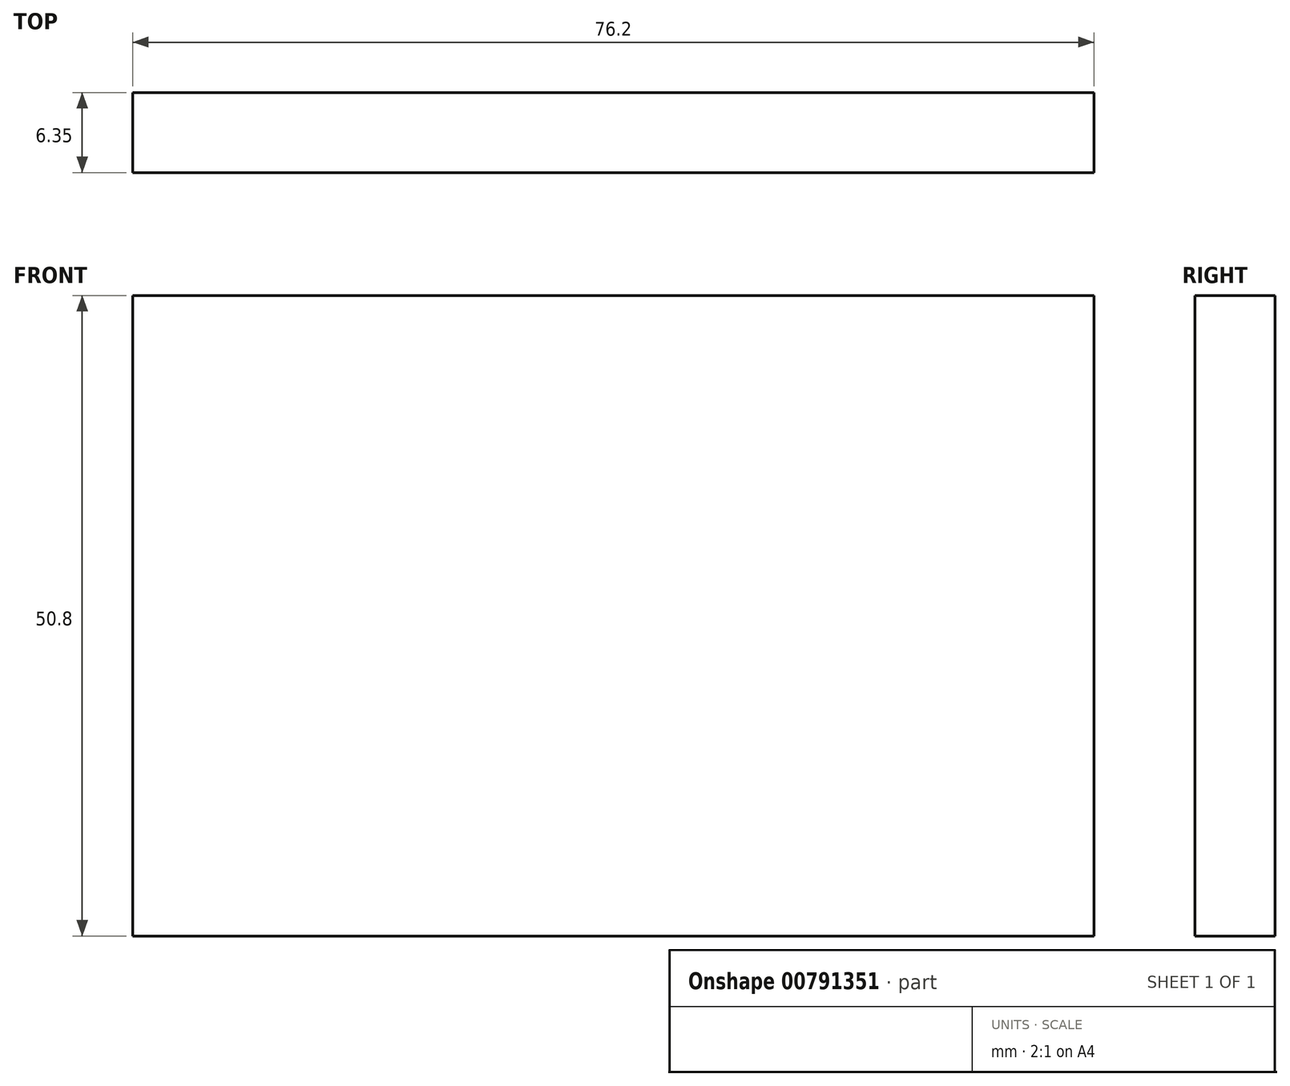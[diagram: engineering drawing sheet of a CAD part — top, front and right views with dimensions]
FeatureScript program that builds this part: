
annotation { "Feature Type Name" : "Feature", "Feature Type Description" : "" }
export const myFeature = defineFeature(function(context is Context, id is Id, definition is map)
    precondition{}
    {
        {
            var Q0;
            Q0=qCreatedBy(makeId("Front.planeOp"),FACE);
            var sketch = newSketch(context, id + "F0", { "sketchPlane" : qUnion([Q0])});
            skLineSegment(sketch, "E0.bottom", {"start": v(0, 0) * mm, "end": v(-76.2, 0) * mm});
            skLineSegment(sketch, "E0.top", {"start": v(0, 50.8) * mm, "end": v(-76.2, 50.8) * mm});
            skLineSegment(sketch, "E0.left", {"start": v(0, 0) * mm, "end": v(0, 50.8) * mm});
            skLineSegment(sketch, "E0.right", {"start": v(-76.2, 0) * mm, "end": v(-76.2, 50.8) * mm});
            skSolve(sketch);
        }
        {
            var Q0;
            Q0 = qSketchRegion(id + "F0", true);
            extrude(context, id + "F1", {"entities" : qUnion([Q0]), "depth" : 6.35 * mm, "offsetDistance" : 25.4 * mm});
        }
    });
